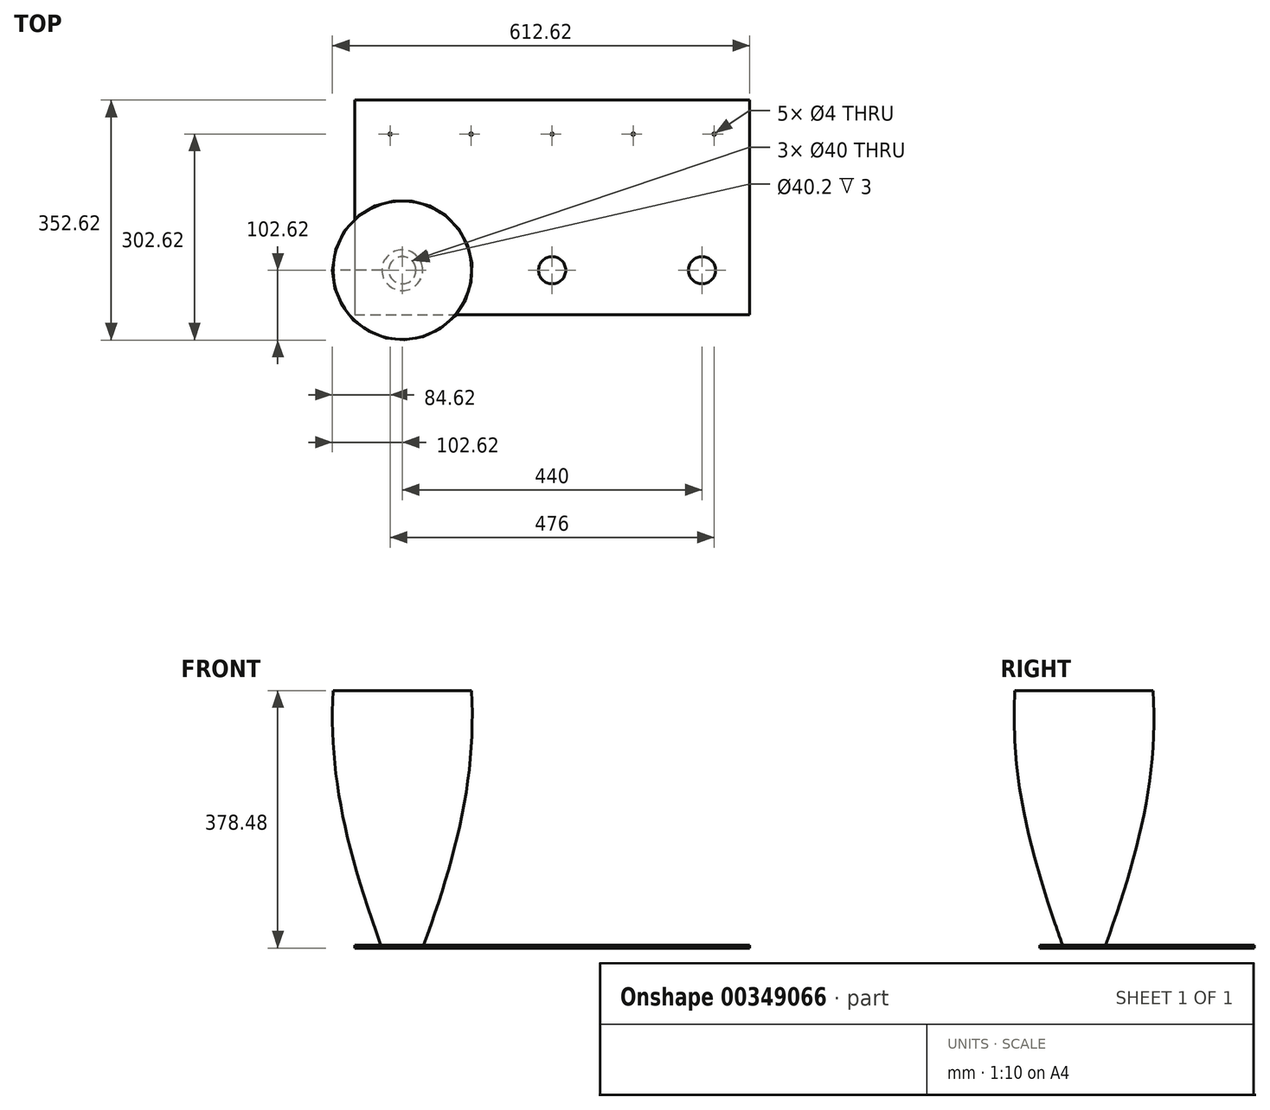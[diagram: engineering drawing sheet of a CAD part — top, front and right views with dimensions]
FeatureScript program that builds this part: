
annotation { "Feature Type Name" : "Feature", "Feature Type Description" : "" }
export const myFeature = defineFeature(function(context is Context, id is Id, definition is map)
    precondition{}
    {
        {
            var Q0;
            Q0=qCreatedBy(makeId("Top.planeOp"),FACE);
            var sketch = newSketch(context, id + "F0", { "sketchPlane" : qUnion([Q0])});
            skCircle(sketch, "E0", {"center": v(0, 0) * mm, "radius": 30 * mm});
            skLineSegment(sketch, "E1", {"start": v(0, 0) * mm, "end": v(40.62, 0) * mm, "construction": true});
            skLineSegment(sketch, "E2", {"start": v(40.62, 0) * mm, "end": v(0, 0) * mm, "construction": true});
            skLineSegment(sketch, "E3", {"start": v(0, 0) * mm, "end": v(0, 34.8) * mm, "construction": true});
            skSolve(sketch);
        }
        {
            var Q0;
            Q0=qSketchRegion(id+"F0",true);
            extrude(context, id + "F1", {"entities" : qUnion([Q0]), "depth" : 3 * mm});
        }
        {
            var Q0;
            Q0=sQuery(id+"F0.wireOp",VERTEX,"E1.start");
            var Q1;
            Q1=makeQuery(id+"F1.opExtrude","SWEPT_BODY",BODY,{"disambiguationData":[OSD([sQuery(id+"F0.wireOp",EDGE,"E0")])]});
            hole(context, id + "F2", {"style" : HoleStyle.SIMPLE, "endStyle" : HoleEndStyle.THROUGH, "oppositeDirection" : true, "holeDiameter" : 40.2 * mm, "isTappedThrough" : true, "tappedDepth" : 12 * mm, "tapClearance" : 3, "locations" : qUnion([Q0]), "scope" : qUnion([Q1])});
        }
        {
            var Q0;
            Q0=qCreatedBy(makeId("Front.planeOp"),FACE);
            var sketch = newSketch(context, id + "F3", { "sketchPlane" : qUnion([Q0])});
            skLineSegment(sketch, "E4", {"start": v(0, 0) * mm, "end": v(0, 95.24) * mm, "construction": true});
            skFitSpline(sketch, "E5", {"points": [v(-29.98, 0) * mm, v(-101.52, 380) * mm], "startDerivative": vector(-164.6, 454.53) * mm, "endDerivative": vector(19.85, 364.4) * mm});
            skFitSpline(sketch, "E6.0", {"points": [v(-28.1, 0.68) * mm, v(-41.8, 38.53) * mm, v(-65.27, 108.65) * mm, v(-88.76, 202.6) * mm, v(-100.75, 290.85) * mm, v(-101.18, 349.6) * mm, v(-99.53, 379.9) * mm]});
            skLineSegment(sketch, "E7", {"start": v(-101.6, 378.48) * mm, "end": v(-99.6, 378.48) * mm});
            skLineSegment(sketch, "E8", {"start": v(-28.45, 1.63) * mm, "end": v(-29.98, 0) * mm});
            skLineSegment(sketch, "E9", {"start": v(0, 95.24) * mm, "end": v(0, 400.08) * mm, "construction": true});
            skLineSegment(sketch, "E10", {"start": v(-101.6, 378.48) * mm, "end": v(0, 378.48) * mm, "construction": true});
            skLineSegment(sketch, "E11", {"start": v(-29.98, 0) * mm, "end": v(0, 0) * mm});
            skLineSegment(sketch, "E12", {"start": v(0, 378.48) * mm, "end": v(-101.6, 378.48) * mm});
            skLineSegment(sketch, "E13", {"start": v(0, 378.48) * mm, "end": v(0, 0) * mm});
            skSolve(sketch);
        }
        {
            var Q0;
            Q0=makeQuery(id+"F3.imprint","IMPRINT",FACE,{"disambiguationData":[TD([[makeQuery(id+"F3.imprint","IMPRINT",EDGE,{"derivedFrom":sQuery(id+"F3.wireOp",EDGE,"E5")}),-1.0]])]});
            var Q1;
            Q1=makeQuery(id+"F3.imprint","IMPRINT",FACE,{"disambiguationData":[TD([[makeQuery(id+"F3.imprint","IMPRINT",EDGE,{"derivedFrom":sQuery(id+"F3.wireOp",EDGE,"E8")}),1.0]])]});
            var Q2;
            Q2=sQuery(id+"F3.wireOp",EDGE,"E6.0");
            var Q3;
            Q3=sQuery(id+"F3.wireOp",EDGE,"E4");
            revolve(context, id + "F4", {"entities" : qUnion([Q0, Q1]), "surfaceEntities" : qUnion([Q2]), "axis" : qUnion([Q3]), "revolveType" : RevolveType.FULL});
        }
        {
            var Q0;
            Q0=qCreatedBy(makeId("Top.planeOp"),FACE);
            var sketch = newSketch(context, id + "F5", { "sketchPlane" : qUnion([Q0])});
            skCircle(sketch, "E14", {"center": v(0, 0) * mm, "radius": 20 * mm});
            skLineSegment(sketch, "E15.bottom", {"start": v(-70, 250) * mm, "end": v(510, 250) * mm});
            skLineSegment(sketch, "E15.top", {"start": v(-70, -65.24) * mm, "end": v(510, -65.24) * mm});
            skLineSegment(sketch, "E15.left", {"start": v(-70, 250) * mm, "end": v(-70, -65.24) * mm});
            skLineSegment(sketch, "E15.right", {"start": v(510, 250) * mm, "end": v(510, -65.24) * mm});
            skCircle(sketch, "E16.1.0.0", {"center": v(220, 0) * mm, "radius": 20 * mm});
            skCircle(sketch, "E16.2.0.0", {"center": v(440, 0) * mm, "radius": 20 * mm});
            skLineSegment(sketch, "E16.direction1", {"start": v(0, 0) * mm, "end": v(220, 0) * mm, "construction": true});
            skLineSegment(sketch, "E17", {"start": v(220, 250) * mm, "end": v(220, -65.24) * mm, "construction": true});
            skPoint(sketch, "E18", {"position": v(220, 200) * mm});
            skPoint(sketch, "E19.1.0.0", {"position": v(339, 200) * mm});
            skPoint(sketch, "E19.2.0.0", {"position": v(458, 200) * mm});
            skLineSegment(sketch, "E19.direction1", {"start": v(220, 200) * mm, "end": v(339, 200) * mm, "construction": true});
            skPoint(sketch, "E20.MirrorP", {"position": v(101, 200) * mm});
            skPoint(sketch, "E21.MirrorP", {"position": v(-18, 200) * mm});
            skSolve(sketch);
        }
        {
            var Q0;
            Q0 = qSketchRegion(id + "F5", true);
            extrude(context, id + "F6", {"entities" : qUnion([Q0]), "depth" : 4 * mm});
        }
        {
            var Q0;
            Q0=sQuery(id+"F5.wireOp",VERTEX,"E21.MirrorP");
            var Q1;
            Q1=sQuery(id+"F5.wireOp",VERTEX,"E20.MirrorP");
            var Q2;
            Q2=sQuery(id+"F5.wireOp",VERTEX,"E18");
            var Q3;
            Q3=sQuery(id+"F5.wireOp",VERTEX,"E19.1.0.0");
            var Q4;
            Q4=sQuery(id+"F5.wireOp",VERTEX,"E19.2.0.0");
            var Q5;
            Q5=makeQuery(id+"F6.opExtrude","SWEPT_BODY",BODY,{"disambiguationData":[OSD([sQuery(id+"F5.wireOp",EDGE,"E14"),sQuery(id+"F5.wireOp",EDGE,"E15.bottom"),sQuery(id+"F5.wireOp",EDGE,"E15.top"),sQuery(id+"F5.wireOp",EDGE,"E15.left"),sQuery(id+"F5.wireOp",EDGE,"E15.right"),sQuery(id+"F5.wireOp",EDGE,"E16.1.0.0"),sQuery(id+"F5.wireOp",EDGE,"E16.2.0.0")])]});
            hole(context, id + "F7", {"style" : HoleStyle.SIMPLE, "endStyle" : HoleEndStyle.THROUGH, "oppositeDirection" : true, "holeDiameter" : 4 * mm, "isTappedThrough" : true, "tappedDepth" : 12 * mm, "tapClearance" : 3, "locations" : qUnion([Q0, Q1, Q2, Q3, Q4]), "scope" : qUnion([Q5])});
        }
    });
